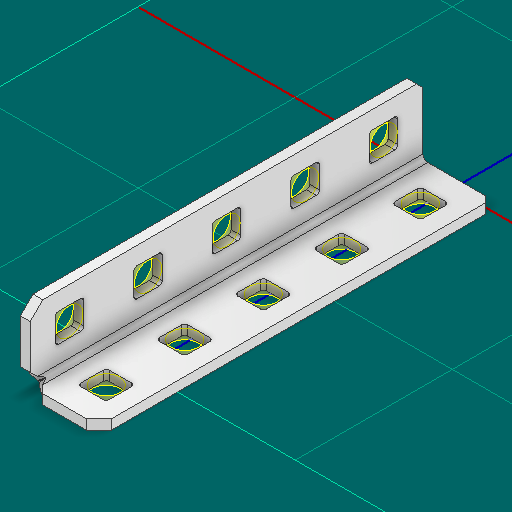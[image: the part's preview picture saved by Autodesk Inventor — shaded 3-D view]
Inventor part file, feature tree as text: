
AUTODESK INVENTOR PART (.ipt)
format: ipt  version: 2025 (Build 290162000, 162)  size: 352,256 bytes
history: native  units: in
note: dims shown in document units (in); Inventor stores cm internally (conversion verified against a paired STEP export)
features: other x29, sketch x2, sheet_metal_op x1
ambient origin geometry x8: Origin, YZ Plane, XZ Plane, XY Plane, X Axis, Y Axis, Z Axis, Center Point
bodies: Solid1 (feature_tree)
feature tree (32):
  other  "Alu Angle 1x1x5.ipt"
  other  "Solid1::Alu Angle 1x1x5.ipt"
  other  "TaggingFeature1"
  sketch  "Sketch1"  dims[d0=0.3937in]
  sketch  "Sketch2"  dims[d1=0.0625in]
  sheet_metal_op  "Body Pattern Sketch"
  other  "Arc Length"
  other  "Diagonal Plane"
  other  "Srf1"
  other  "Srf2"
  other  "Srf3"
  other  "Srf4"
  other  "Srf5"
  other  "Srf6"
  other  "Srf7"
  other  "Srf8"
  other  "Srf9"
  other  "Srf10"
  other  "Srf11"
  other  "Srf12"
  other  "Srf91::Derived"
  other  "Srf92::Derived"
  other  "Srf856::Derived"
  other  "Srf857::Derived"
  other  "Srf858::Derived"
  other  "Srf859::Derived"
  other  "Srf1275::Derived"
  other  "Srf1276::Derived"
  other  "Srf1278::Derived"
  other  "Srf1279::Derived"
  other  "Srf1280::Derived"
  other  "Srf1281::Derived"
